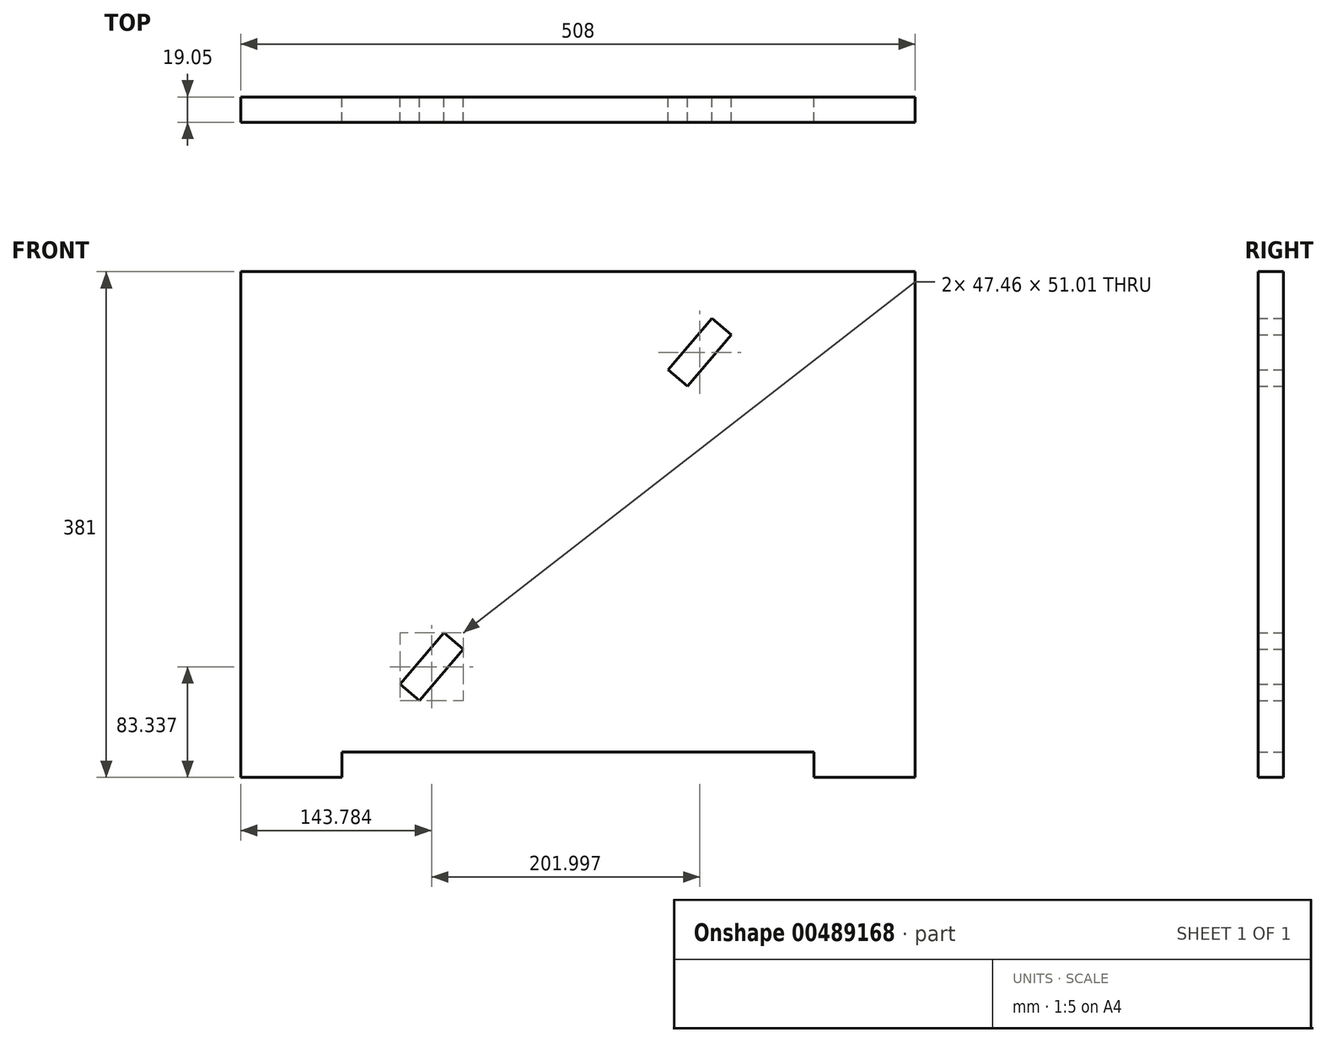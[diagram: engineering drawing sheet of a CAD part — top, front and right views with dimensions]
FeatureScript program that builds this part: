
annotation { "Feature Type Name" : "Feature", "Feature Type Description" : "" }
export const myFeature = defineFeature(function(context is Context, id is Id, definition is map)
    precondition{}
    {
        {
            var Q0;
            Q0=qCreatedBy(makeId("Front.planeOp"),FACE);
            var sketch = newSketch(context, id + "F0", { "sketchPlane" : qUnion([Q0])});
            skLineSegment(sketch, "E0.bottom", {"start": v(-227.7, 261.14) * mm, "end": v(280.3, 261.14) * mm});
            skLineSegment(sketch, "E0.top", {"start": v(-227.7, -100.8) * mm, "end": v(280.3, -100.8) * mm});
            skLineSegment(sketch, "E0.left", {"start": v(-227.7, 261.14) * mm, "end": v(-227.7, -100.8) * mm});
            skLineSegment(sketch, "E0.right", {"start": v(280.3, 261.14) * mm, "end": v(280.3, -100.8) * mm});
            skLineSegment(sketch, "E1.bottom", {"start": v(-227.7, -100.8) * mm, "end": v(-151.5, -100.8) * mm});
            skLineSegment(sketch, "E1.top", {"start": v(-227.7, -119.86) * mm, "end": v(-151.5, -119.86) * mm});
            skLineSegment(sketch, "E1.left", {"start": v(-227.7, -100.8) * mm, "end": v(-227.7, -119.86) * mm});
            skLineSegment(sketch, "E1.right", {"start": v(-151.5, -100.8) * mm, "end": v(-151.5, -119.86) * mm});
            skLineSegment(sketch, "E2.bottom", {"start": v(280.3, -100.8) * mm, "end": v(204.1, -100.8) * mm});
            skLineSegment(sketch, "E2.top", {"start": v(280.3, -119.86) * mm, "end": v(204.1, -119.86) * mm});
            skLineSegment(sketch, "E2.left", {"start": v(280.3, -100.8) * mm, "end": v(280.3, -119.86) * mm});
            skLineSegment(sketch, "E2.right", {"start": v(204.1, -100.8) * mm, "end": v(204.1, -119.86) * mm});
            skLineSegment(sketch, "E3", {"start": v(127.32, 225.8) * mm, "end": v(141.81, 213.45) * mm});
            skLineSegment(sketch, "E4", {"start": v(141.81, 213.45) * mm, "end": v(108.85, 174.8) * mm});
            skLineSegment(sketch, "E5", {"start": v(108.85, 174.8) * mm, "end": v(94.35, 187.16) * mm});
            skLineSegment(sketch, "E6", {"start": v(94.35, 187.16) * mm, "end": v(127.32, 225.8) * mm});
            skLineSegment(sketch, "E7", {"start": v(-60.19, -23.38) * mm, "end": v(-93.15, -62.03) * mm});
            skLineSegment(sketch, "E8", {"start": v(-74.68, -11.02) * mm, "end": v(-107.65, -49.67) * mm});
            skLineSegment(sketch, "E9", {"start": v(-60.19, -23.38) * mm, "end": v(-74.68, -11.02) * mm});
            skLineSegment(sketch, "E10", {"start": v(-107.65, -49.67) * mm, "end": v(-93.15, -62.03) * mm});
            skSolve(sketch);
        }
        {
            var Q0;
            Q0 = qSketchRegion(id + "F0", true);
            extrude(context, id + "F1", {"entities" : qUnion([Q0]), "depth" : 19.05 * mm});
        }
    });
